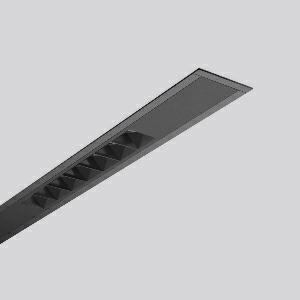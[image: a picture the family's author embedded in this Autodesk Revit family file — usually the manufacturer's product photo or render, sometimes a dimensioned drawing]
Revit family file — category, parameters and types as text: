
# Revit family: less_is_more_beamline_312480_003_942f
name_source: partatom
category: Lighting Fixtures
units: mm (PartAtom-declared; Revit-internal decimal feet)

## family parameters
Cut with Voids When Loaded = No
Host = Face
Light Source = No
Part Type = Normal
Room Calculation Point = No
Round Connector Dimension = Use Diameter
Shared = No

## types (1)
- LESS IS MORE BEAMLINE (1 x LED Modul 930, 1800 lm, 3000)
    Apparent Load = 97 VA
    CIE Flux Codes = 100 100 100 100 100
    Color Rendering = 90
    Color Temperature = 3000
    Default Elevation = 1800 mm  [stored 5.90551 ft]
    Description = Series: LESS IS MORE BEAMLINE
Linear recessed ceiling and wall luminaire for aesthetically sophisticated lighting. Luminaire with four LED light units. Housing: extruded aluminium profile, powder-coated. End cap aluminium powder-coated. LED light unit with MRS technology: Mini-Reflector-System made of metallised thermoplastic with prismatic black glare-suppressing frame for pleasant glare-free light (RUG < 10). Each LED light unit has 7 reflector elements. Narrow beam light distribution. Ceiling installation with pre-assembled SBS mounting system. LED unit with integrated converter interchangeable and removable. Suitable for through-wiring. 
Colour: deep black, matt (RAL 9005)
Length: 2262 mm
Width: 71 mm
Height: 1.5 mm
Cut-out length: 2243 mm
Cut-out width: 60 mm
Recess height: 125 mm
Luminaire: recess height: 106 mm
Lamp: LED
Socket: without socket
Colour temperature: 3000K
Colour rendering index (CRI): 90
System power: 97 W
Rated luminous flux: 7200 lm
Luminous efficiency: 74 lm/W
Control gear: Regulated power supply
Protection class: I
Type of protection: IP 20
    Height = 0 mm  [stored 0 ft]
    Lamp = 1 x LED Modul 930
    Lamp Light Flux = 1800 lm
    Lamp count = 1
    Length = 2262 mm
    Lifetime = 50000 h
    Luminous efficacy = 74 lm/W
    Manufacturer = RZB
    ModVariant = No
    Model = 312480.003
    Mounting Place = Ceiling, Wall
    Mounting Type = Recessed
    Number of Poles = 1
    OnlyDefault = Yes
    Power Factor = 1
    Product Name = LESS IS MORE BEAMLINE
    Product group = Recessed LED linear luminaires
    ProductGroupID = 407
    Protection Class = Protection class I
    Protection Degree = IP 20
    RLX_Detail_Level = 1
    RLX_Emergency_Light_Flux = 0 lm
    RLX_Emergency_Type = 0
    RLX_Emergency_Type_DB = No
    RlxData = <blob elided: 24681 chars, md5=c7ed2fda>
    Socket = socket
    Standby Power = 0 W
    System Light Flux = 7200 lm
    System Power = 97 W
    Type Comments = Product without accessories
    Type Image = 312465.003.jpg
    URL = http://relux.com
    VarID = ---
    Voltage = 230 V
    Voltage Range = 220-240 V
    Weight = 0.00 kg
    Width = 71 mm

note: [stored X ft] marks values corroborated as IEEE doubles in the binary element streams (Revit-internal decimal feet)

## geometry (parser evidence)
native form markers: Blend x4, Sweep x21
no freeform markers — native parametric forms only
